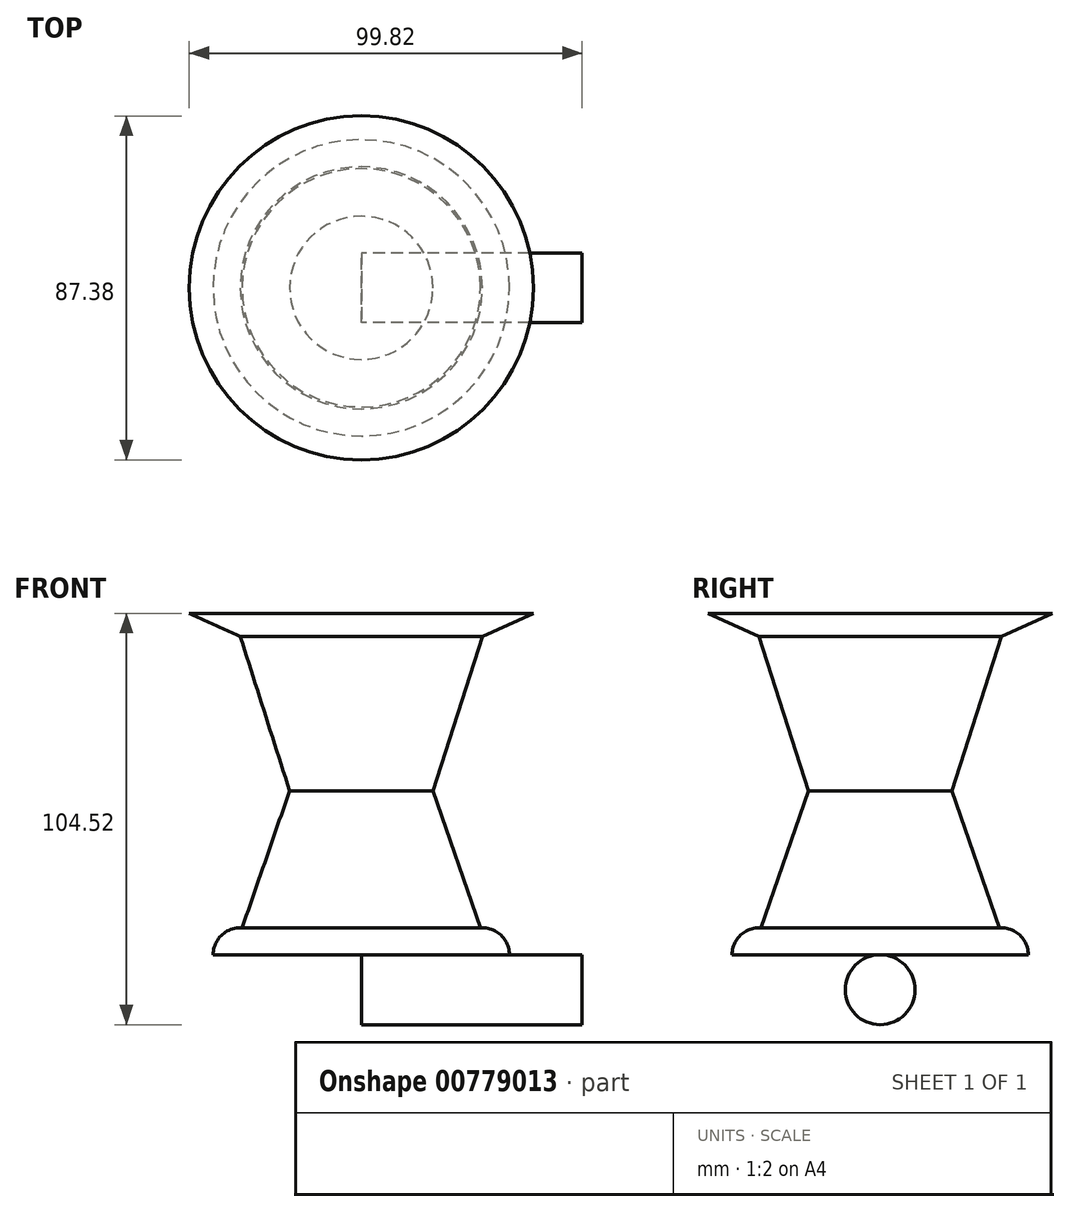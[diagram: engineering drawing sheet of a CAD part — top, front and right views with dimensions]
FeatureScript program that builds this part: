
annotation { "Feature Type Name" : "Feature", "Feature Type Description" : "" }
export const myFeature = defineFeature(function(context is Context, id is Id, definition is map)
    precondition{}
    {
        {
            var Q0;
            Q0=qCreatedBy(makeId("Front.planeOp"),FACE);
            var sketch = newSketch(context, id + "F0", { "sketchPlane" : qUnion([Q0])});
            skLineSegment(sketch, "E0", {"start": v(0, 0) * mm, "end": v(37.64, 0) * mm});
            skArc(sketch, "E1", {"start": v(37.64, 0) * mm, "mid": v(35.45, 5.04) * mm, "end": v(30.27, 6.87) * mm});
            skLineSegment(sketch, "E2", {"start": v(30.27, 6.87) * mm, "end": v(18.2, 41.65) * mm});
            skLineSegment(sketch, "E3", {"start": v(18.2, 41.65) * mm, "end": v(30.75, 80.92) * mm});
            skLineSegment(sketch, "E4", {"start": v(30.75, 80.92) * mm, "end": v(43.7, 86.78) * mm});
            skLineSegment(sketch, "E5", {"start": v(43.7, 86.78) * mm, "end": v(0, 86.78) * mm});
            skLineSegment(sketch, "E6", {"start": v(0, 86.78) * mm, "end": v(0, 0) * mm});
            skLineSegment(sketch, "E7", {"start": v(0, 86.78) * mm, "end": v(0, 120.49) * mm, "construction": true});
            skSolve(sketch);
        }
        {
            var Q0;
            Q0 = qSketchRegion(id + "F0", true);
            var Q1;
            Q1=sQuery(id+"F0.wireOp",EDGE,"E7");
            revolve(context, id + "F1", {"surfaceOperationType" : NewSurfaceOperationType.NEW, "entities" : qUnion([Q0]), "axis" : qUnion([Q1]), "revolveType" : RevolveType.FULL});
        }
        {
            var Q0;
            Q0=qCreatedBy(makeId("Front.planeOp"),FACE);
            var sketch = newSketch(context, id + "F2", { "sketchPlane" : qUnion([Q0])});
            skLineSegment(sketch, "E8.bottom", {"start": v(0, 0) * mm, "end": v(56.13, 0) * mm});
            skLineSegment(sketch, "E8.top", {"start": v(0, -8.87) * mm, "end": v(56.13, -8.87) * mm});
            skLineSegment(sketch, "E8.left", {"start": v(0, 0) * mm, "end": v(0, -8.87) * mm});
            skLineSegment(sketch, "E8.right", {"start": v(56.13, 0) * mm, "end": v(56.13, -8.87) * mm});
            skLineSegment(sketch, "E9", {"start": v(0, -30.21) * mm, "end": v(0, 97.84) * mm, "construction": true});
            skPoint(sketch, "E9.endSnap0", {"position": v(0, -4.43) * mm});
            skSolve(sketch);
        }
        {
            var Q0;
            Q0 = qSketchRegion(id + "F2", true);
            var Q1;
            Q1=sQuery(id+"F2.wireOp",EDGE,"E8.top");
            revolve(context, id + "F3", {"surfaceOperationType" : NewSurfaceOperationType.NEW, "entities" : qUnion([Q0]), "axis" : qUnion([Q1]), "revolveType" : RevolveType.FULL});
        }
    });
